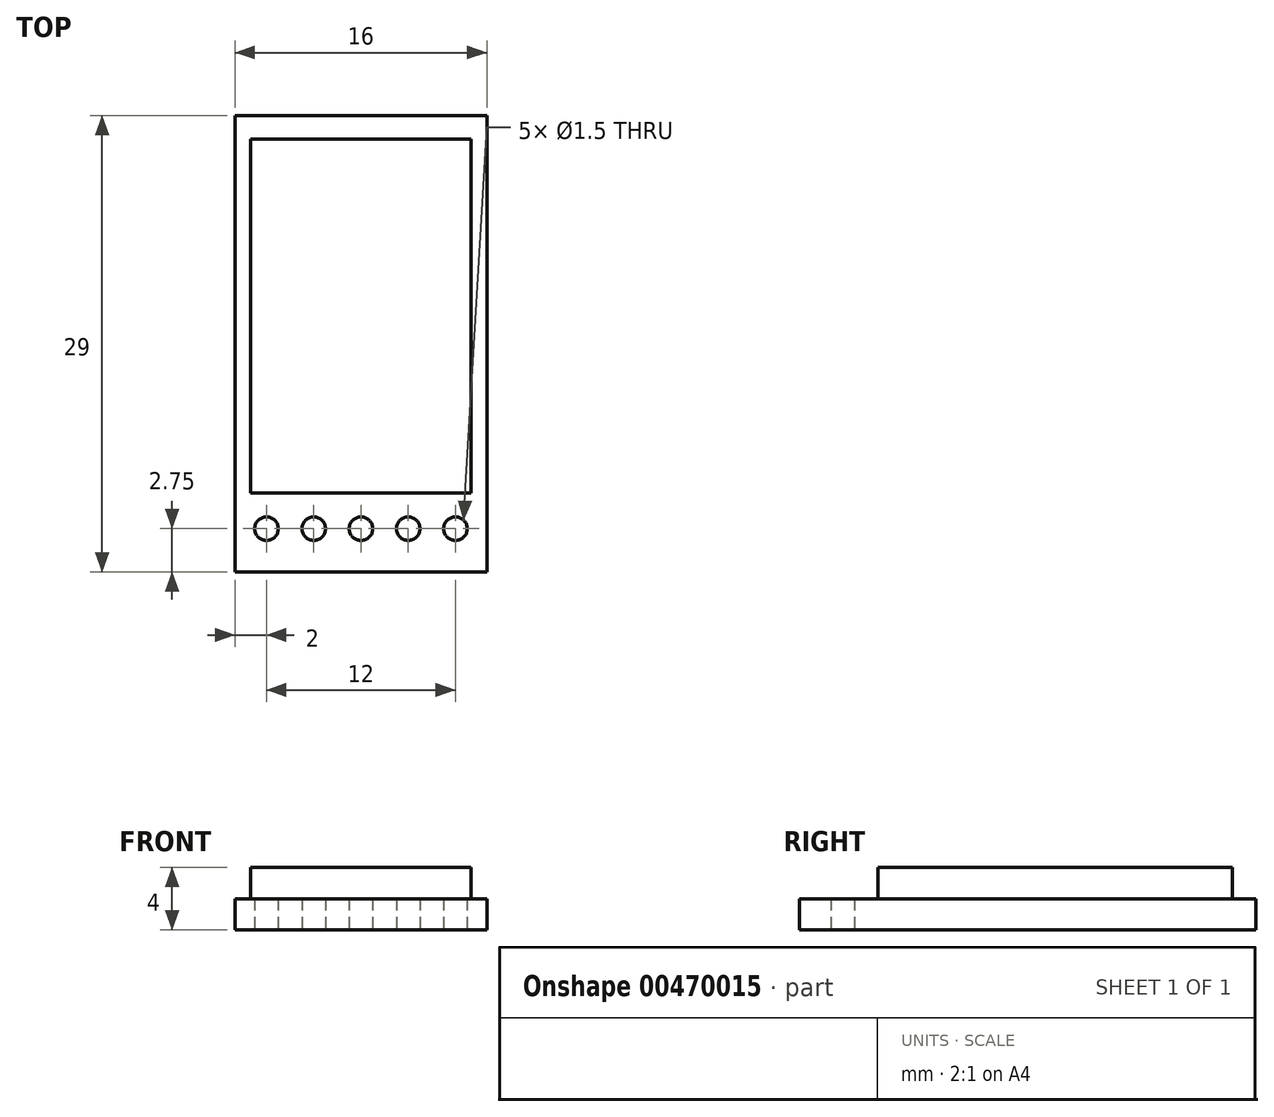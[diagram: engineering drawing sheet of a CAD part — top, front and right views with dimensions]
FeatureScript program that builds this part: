
annotation { "Feature Type Name" : "Feature", "Feature Type Description" : "" }
export const myFeature = defineFeature(function(context is Context, id is Id, definition is map)
    precondition{}
    {
        {
            var Q0;
            Q0=qCreatedBy(makeId("Top.planeOp"),FACE);
            var sketch = newSketch(context, id + "F0", { "sketchPlane" : qUnion([Q0])});
            skLineSegment(sketch, "E0.bottom", {"start": v(8, -14.5) * mm, "end": v(-8, -14.5) * mm});
            skLineSegment(sketch, "E0.top", {"start": v(8, 14.5) * mm, "end": v(-8, 14.5) * mm});
            skLineSegment(sketch, "E0.left", {"start": v(8, -14.5) * mm, "end": v(8, 14.5) * mm});
            skLineSegment(sketch, "E0.right", {"start": v(-8, -14.5) * mm, "end": v(-8, 14.5) * mm});
            skPoint(sketch, "E0.middle", {"position": v(0, 0) * mm});
            skCircle(sketch, "E1", {"center": v(0, -11.75) * mm, "radius": 0.75 * mm});
            skCircle(sketch, "E2", {"center": v(-3, -11.75) * mm, "radius": 0.75 * mm});
            skCircle(sketch, "E3", {"center": v(-6, -11.75) * mm, "radius": 0.75 * mm});
            skCircle(sketch, "E4.MirrorC", {"center": v(3, -11.75) * mm, "radius": 0.75 * mm});
            skCircle(sketch, "E5.MirrorC", {"center": v(6, -11.75) * mm, "radius": 0.75 * mm});
            skLineSegment(sketch, "E6.bottom", {"start": v(-7, 13) * mm, "end": v(7, 13) * mm});
            skLineSegment(sketch, "E6.top", {"start": v(-7, -9.5) * mm, "end": v(7, -9.5) * mm});
            skLineSegment(sketch, "E6.left", {"start": v(-7, 13) * mm, "end": v(-7, -9.5) * mm});
            skLineSegment(sketch, "E6.right", {"start": v(7, 13) * mm, "end": v(7, -9.5) * mm});
            skSolve(sketch);
        }
        {
            var Q0;
            Q0 = qSketchRegion(id + "F0", true);
            extrude(context, id + "F1", {"entities" : qUnion([Q0]), "depth" : 2 * mm, "offsetDistance" : 25 * mm});
        }
        {
            var Q0;
            Q0=makeQuery(id+"F0.imprint","IMPRINT",FACE,{"disambiguationData":[TD([[makeQuery(id+"F0.imprint","IMPRINT",EDGE,{"derivedFrom":sQuery(id+"F0.wireOp",EDGE,"E6.bottom")}),-1.0]])]});
            extrude(context, id + "F2", {"entities" : qUnion([Q0]), "operationType" : NewBodyOperationType.ADD, "depth" : 4 * mm, "offsetDistance" : 25 * mm});
        }
    });
